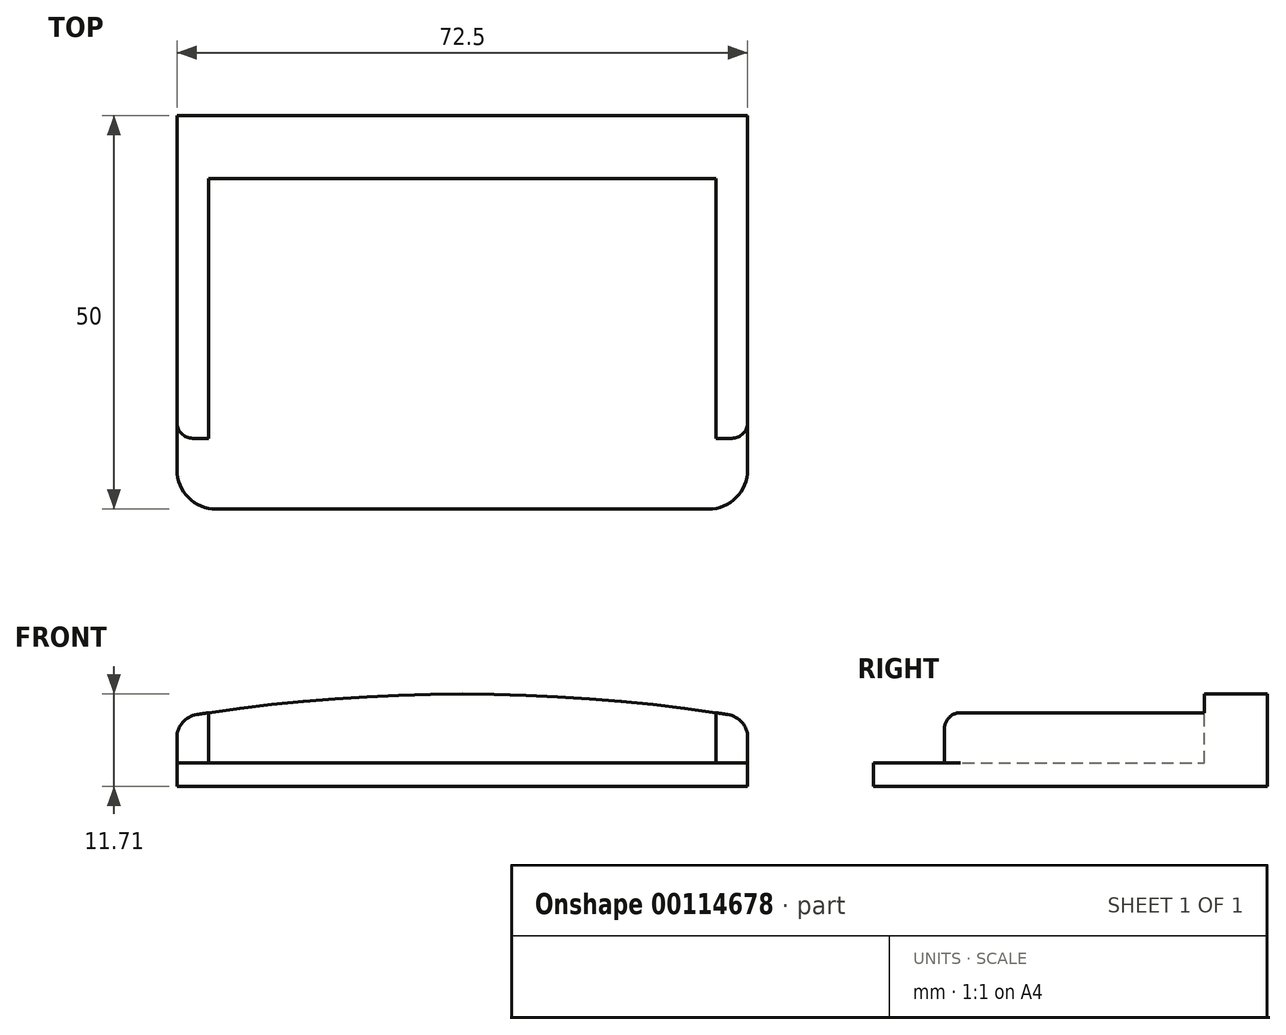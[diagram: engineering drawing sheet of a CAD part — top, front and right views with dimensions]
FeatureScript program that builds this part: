
annotation { "Feature Type Name" : "Feature", "Feature Type Description" : "" }
export const myFeature = defineFeature(function(context is Context, id is Id, definition is map)
    precondition{}
    {
        {
            var Q0;
            Q0=qCreatedBy(makeId("Top.planeOp"),FACE);
            var sketch = newSketch(context, id + "F0", { "sketchPlane" : qUnion([Q0])});
            skLineSegment(sketch, "E0.bottom", {"start": v(-36.25, 25) * mm, "end": v(36.25, 25) * mm});
            skLineSegment(sketch, "E0.top", {"start": v(-36.25, -25) * mm, "end": v(36.25, -25) * mm});
            skLineSegment(sketch, "E0.left", {"start": v(-36.25, 25) * mm, "end": v(-36.25, -25) * mm});
            skLineSegment(sketch, "E0.right", {"start": v(36.25, 25) * mm, "end": v(36.25, -25) * mm});
            skSolve(sketch);
        }
        {
            var Q0;
            Q0=makeQuery(id+"F0.imprint","IMPRINT",FACE,{"disambiguationData":[TD([[makeQuery(id+"F0.imprint","IMPRINT",EDGE,{"derivedFrom":sQuery(id+"F0.wireOp",EDGE,"E0.bottom")}),-1.0]])]});
            extrude(context, id + "F1", {"entities" : qUnion([Q0]), "depth" : 3 * mm});
        }
        {
            var Q0;
            Q0=makeQuery(id+"F1.opExtrude","SWEPT_EDGE",EDGE,{"disambiguationData":[OSD([sQuery(id+"F0.wireOp",EDGE,"E0.top"),sQuery(id+"F0.wireOp",EDGE,"E0.right")])]});
            var Q1;
            Q1=makeQuery(id+"F1.opExtrude","SWEPT_EDGE",EDGE,{"disambiguationData":[OSD([sQuery(id+"F0.wireOp",EDGE,"E0.top"),sQuery(id+"F0.wireOp",EDGE,"E0.left")])]});
            fillet(context, id + "F2", {"entities" : qUnion([Q0, Q1]), "radius" : 5 * mm, "tangentPropagation" : true, "allowEdgeOverflow" : false});
        }
        {
            var Q0;
            Q0=makeQuery(id+"F1.opExtrude","SWEPT_FACE",FACE,{"disambiguationData":[OSD([sQuery(id+"F0.wireOp",EDGE,"E0.bottom")])]});
            var sketch = newSketch(context, id + "F3", { "sketchPlane" : qUnion([Q0])});
            skPoint(sketch, "E1.endSnap0", {"position": v(0, 11.71) * mm});
            skArc(sketch, "E2", {"start": v(36.25, 8.71) * mm, "mid": v(0, 11.71) * mm, "end": v(-36.25, 8.71) * mm});
            skPoint(sketch, "E1.end.orphan", {"position": v(0, 15.33) * mm});
            skPoint(sketch, "E1.start.orphan", {"position": v(0, 11.71) * mm});
            skPoint(sketch, "E3.start.orphan", {"position": v(36.25, 11.71) * mm});
            skPoint(sketch, "E4.start.orphan", {"position": v(-36.25, 11.71) * mm});
            skLineSegment(sketch, "E5", {"start": v(-36.25, 8.71) * mm, "end": v(-36.25, 3) * mm});
            skLineSegment(sketch, "E6", {"start": v(36.25, 8.71) * mm, "end": v(36.25, 3) * mm});
            skLineSegment(sketch, "E7", {"start": v(36.25, 3) * mm, "end": v(-36.25, 3) * mm});
            skSolve(sketch);
        }
        {
            var Q0;
            Q0=makeQuery(id+"F3.imprint","IMPRINT",FACE,{"disambiguationData":[TD([[makeQuery(id+"F3.imprint","IMPRINT",EDGE,{"derivedFrom":sQuery(id+"F3.wireOp",EDGE,"E2")}),1.0]])]});
            extrude(context, id + "F4", {"entities" : qUnion([Q0]), "operationType" : NewBodyOperationType.ADD, "oppositeDirection" : true, "depth" : 8 * mm});
        }
        {
            var Q0;
            Q0=makeQuery(id+"F4.opExtrude","SWEPT_EDGE",EDGE,{"disambiguationData":[OSD([sQuery(id+"F3.wireOp",EDGE,"E2"),sQuery(id+"F3.wireOp",EDGE,"E5")])]});
            var Q1;
            Q1=makeQuery(id+"F4.opExtrude","SWEPT_EDGE",EDGE,{"disambiguationData":[OSD([sQuery(id+"F3.wireOp",EDGE,"E2"),sQuery(id+"F3.wireOp",EDGE,"E6")])]});
            fillet(context, id + "F5", {"entities" : qUnion([Q0, Q1]), "radius" : 3 * mm, "tangentPropagation" : true, "allowEdgeOverflow" : false});
        }
        {
            var Q0;
            Q0=makeQuery(id+"F4.opExtrude","CAP_FACE",FACE,{"disambiguationData":[OSD([sQuery(id+"F3.wireOp",EDGE,"E2"),sQuery(id+"F3.wireOp",EDGE,"E5"),sQuery(id+"F3.wireOp",EDGE,"E6"),sQuery(id+"F3.wireOp",EDGE,"E7")])],"isStart":false});
            var sketch = newSketch(context, id + "F6", { "sketchPlane" : qUnion([Q0])});
            skLineSegment(sketch, "E8", {"start": v(36.25, 3) * mm, "end": v(32.25, 3) * mm});
            skLineSegment(sketch, "E9", {"start": v(32.25, 3) * mm, "end": v(32.25, 9.34) * mm});
            skSolve(sketch);
        }
        {
            var Q0;
            Q0=makeQuery(id+"F6.imprint","IMPRINT",FACE,{"disambiguationData":[TD([[makeQuery(id+"F6.imprint","IMPRINT",EDGE,{"derivedFrom":sQuery(id+"F6.wireOp",EDGE,"E8")}),1.0]])]});
            extrude(context, id + "F7", {"entities" : qUnion([Q0]), "operationType" : NewBodyOperationType.ADD, "depth" : 33 * mm});
        }
        {
            var Q0;
            Q0=makeQuery(id+"F7.opExtrude","CAP_EDGE",EDGE,{"disambiguationData":[OSD([sQuery(id+"F3.wireOp",EDGE,"E5")])],"isStart":false});
            fillet(context, id + "F8", {"entities" : qUnion([Q0]), "radius" : 2 * mm, "tangentPropagation" : true, "allowEdgeOverflow" : false});
        }
        {
            var Q0;
            Q0=makeQuery(id+"F1.opExtrude","SWEPT_BODY",BODY,{"disambiguationData":[OSD([sQuery(id+"F0.wireOp",EDGE,"E0.bottom"),sQuery(id+"F0.wireOp",EDGE,"E0.top"),sQuery(id+"F0.wireOp",EDGE,"E0.left"),sQuery(id+"F0.wireOp",EDGE,"E0.right")])]});
            var Q1;
            Q1=qCreatedBy(makeId("Right.planeOp"),FACE);
            mirror(context, id + "F9", {"operationType" : NewBodyOperationType.ADD, "entities" : qUnion([Q0]), "mirrorPlane" : qUnion([Q1])});
        }
    });
